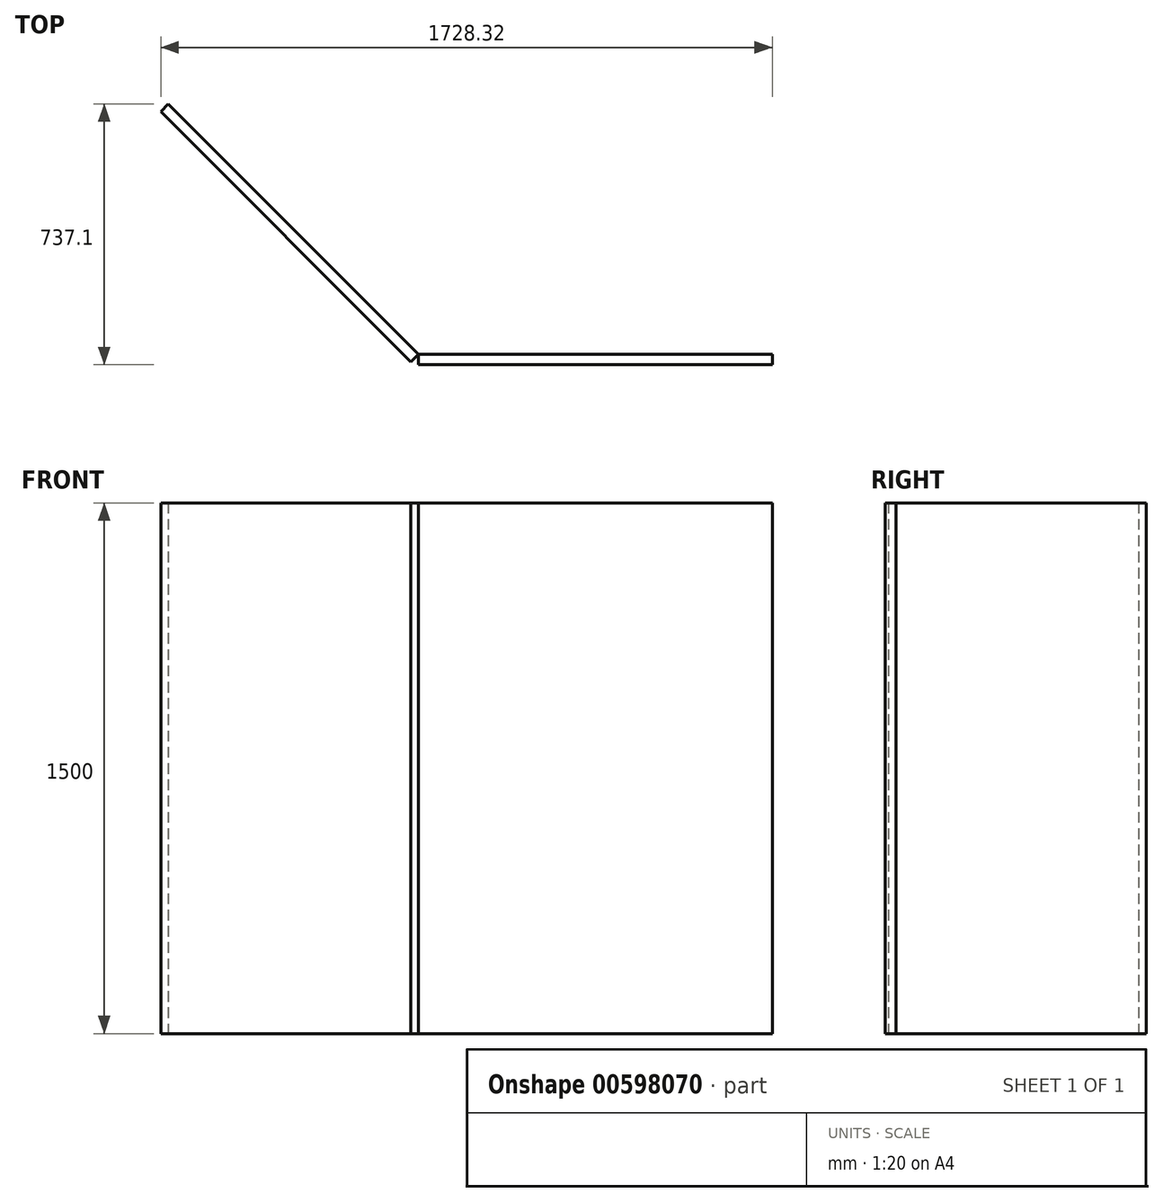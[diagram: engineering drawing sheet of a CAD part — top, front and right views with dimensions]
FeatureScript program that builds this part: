
annotation { "Feature Type Name" : "Feature", "Feature Type Description" : "" }
export const myFeature = defineFeature(function(context is Context, id is Id, definition is map)
    precondition{}
    {
        {
            var Q0;
            Q0=qCreatedBy(makeId("Top.planeOp"),FACE);
            var sketch = newSketch(context, id + "F0", { "sketchPlane" : qUnion([Q0])});
            skLineSegment(sketch, "E0.bottom", {"start": v(-156.9, -228.84) * mm, "end": v(843.1, -228.84) * mm});
            skLineSegment(sketch, "E0.top", {"start": v(-156.9, -258.84) * mm, "end": v(843.1, -258.84) * mm});
            skLineSegment(sketch, "E0.left", {"start": v(-156.9, -228.84) * mm, "end": v(-156.9, -258.84) * mm});
            skLineSegment(sketch, "E0.right", {"start": v(843.1, -228.84) * mm, "end": v(843.1, -258.84) * mm});
            skLineSegment(sketch, "E1", {"start": v(-156.9, -228.84) * mm, "end": v(-864.01, 478.26) * mm});
            skLineSegment(sketch, "E2", {"start": v(-864.01, 478.26) * mm, "end": v(-885.22, 457.05) * mm});
            skLineSegment(sketch, "E3", {"start": v(-885.22, 457.05) * mm, "end": v(-178.12, -250.06) * mm});
            skLineSegment(sketch, "E4", {"start": v(-178.12, -250.06) * mm, "end": v(-156.9, -228.84) * mm});
            skSolve(sketch);
        }
        {
            var Q0;
            Q0 = qSketchRegion(id + "F0", true);
            extrude(context, id + "F1", {"entities" : qUnion([Q0]), "depth" : 1500 * mm, "offsetDistance" : 25 * mm});
        }
    });
